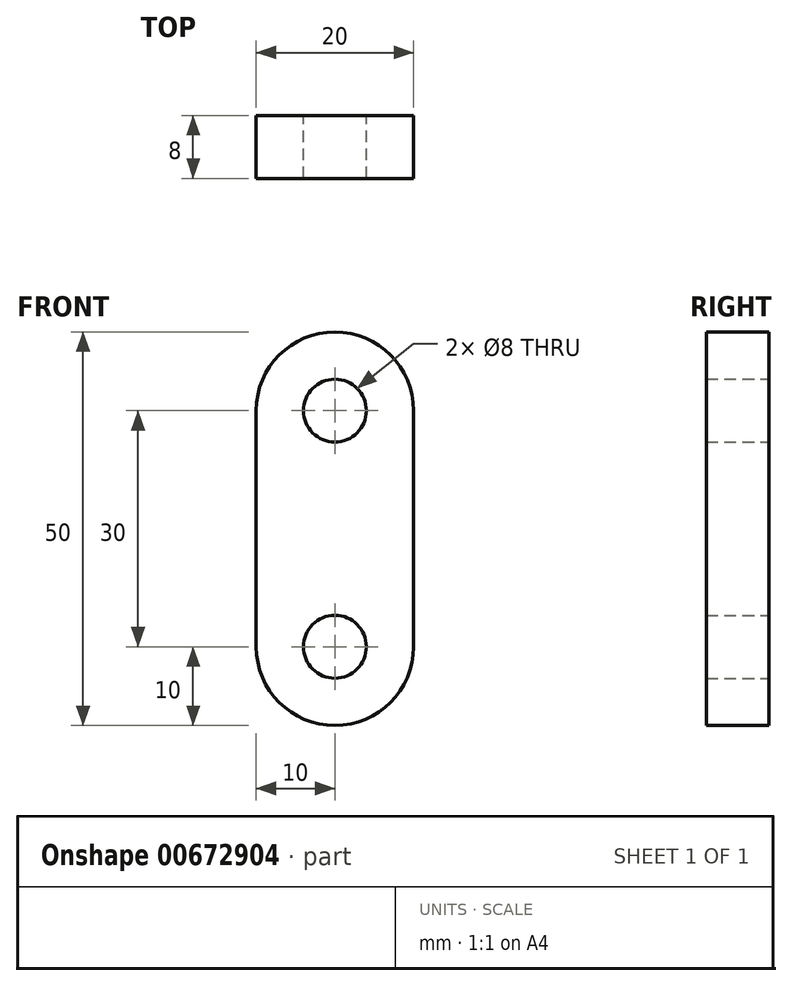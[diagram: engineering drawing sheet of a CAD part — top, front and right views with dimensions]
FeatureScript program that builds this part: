
annotation { "Feature Type Name" : "Feature", "Feature Type Description" : "" }
export const myFeature = defineFeature(function(context is Context, id is Id, definition is map)
    precondition{}
    {
        {
            var Q0;
            Q0=qCreatedBy(makeId("Front.planeOp"),FACE);
            var sketch = newSketch(context, id + "F0", { "sketchPlane" : qUnion([Q0])});
            skArc(sketch, "E0", {"start": v(-10, 0) * mm, "mid": v(0, -10) * mm, "end": v(10, 0) * mm});
            skArc(sketch, "E1", {"start": v(10, 30) * mm, "mid": v(0, 40) * mm, "end": v(-10, 30) * mm});
            skCircle(sketch, "E2", {"center": v(0, 0) * mm, "radius": 4 * mm});
            skCircle(sketch, "E3", {"center": v(0, 30) * mm, "radius": 4 * mm});
            skLineSegment(sketch, "E4", {"start": v(10, 30) * mm, "end": v(10, 0) * mm});
            skLineSegment(sketch, "E5", {"start": v(-10, 30) * mm, "end": v(-10, 0) * mm});
            skSolve(sketch);
        }
        {
            var Q0;
            Q0 = qSketchRegion(id + "F0", true);
            extrude(context, id + "F1", {"entities" : qUnion([Q0]), "depth" : 8 * mm, "offsetDistance" : 25 * mm});
        }
    });
